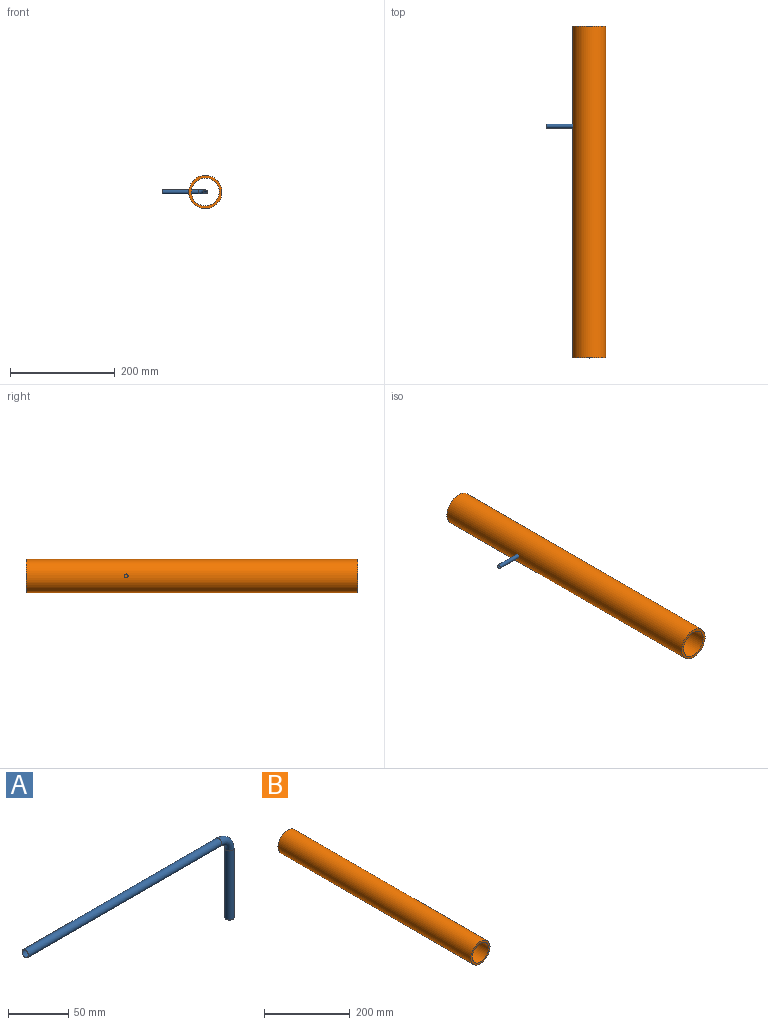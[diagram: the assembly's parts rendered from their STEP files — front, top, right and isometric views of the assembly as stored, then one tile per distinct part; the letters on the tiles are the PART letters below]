
ASSEMBLY  parts=2 mates=1
PART A: 8 faces, bbox 244.5x7.6x88.1 mm
  f0: cylinder r=3.6mm len=226.68mm, axis (1,0,0), area 5128.1mm2, adj f1,f3
  f1: torus R=12.7mm, axis (0,1,0), area 451.3mm2, adj f0,f2
  f2: cylinder r=3.6mm len=70.18mm, axis (0,0,-1), area 1587.8mm2, adj f1,f4
  f3: plane 7.62x7.62mm, normal (-1,0,0), area 4.9mm2, adj f0,f5
  f4: plane 7.62x7.62mm, normal (0,0,-1), area 4.9mm2, adj f2,f7
  f5: cylinder r=3.81mm len=226.68mm, axis (1,0,0), area 5426.4mm2, adj f3,f6
  f6: torus R=12.7mm, axis (0,1,0), area 477.6mm2, adj f5,f7
  f7: cylinder r=3.81mm len=70.18mm, axis (0,0,-1), area 1680.1mm2, adj f4,f6
PART B: 4 faces, bbox 63.5x635x63.5 mm
  f0: cylinder r=26.67mm len=635mm, axis (0,1,0), area 106408.6mm2, adj f2,f3
  f1: cylinder r=31.75mm len=635mm, axis (0,1,0), area 126676.9mm2, adj f2,f3
  f2: plane 63.5x63.5mm, normal (0,-1,0), area 932.3mm2, adj f0,f1
  f3: plane 63.5x63.5mm, normal (0,1,0), area 932.3mm2, adj f0,f1
PLACE A rot(axis=(0.58,0.58,0.58),120deg) t=(-100.17,-168.07,-202.46)mm
PLACE B t=(-100.17,126.12,-202.46)mm
MATE fastened A.f5 <-> B.f1  axis (0,1,0) through (-100.17,-191.38,-202.46)mm
